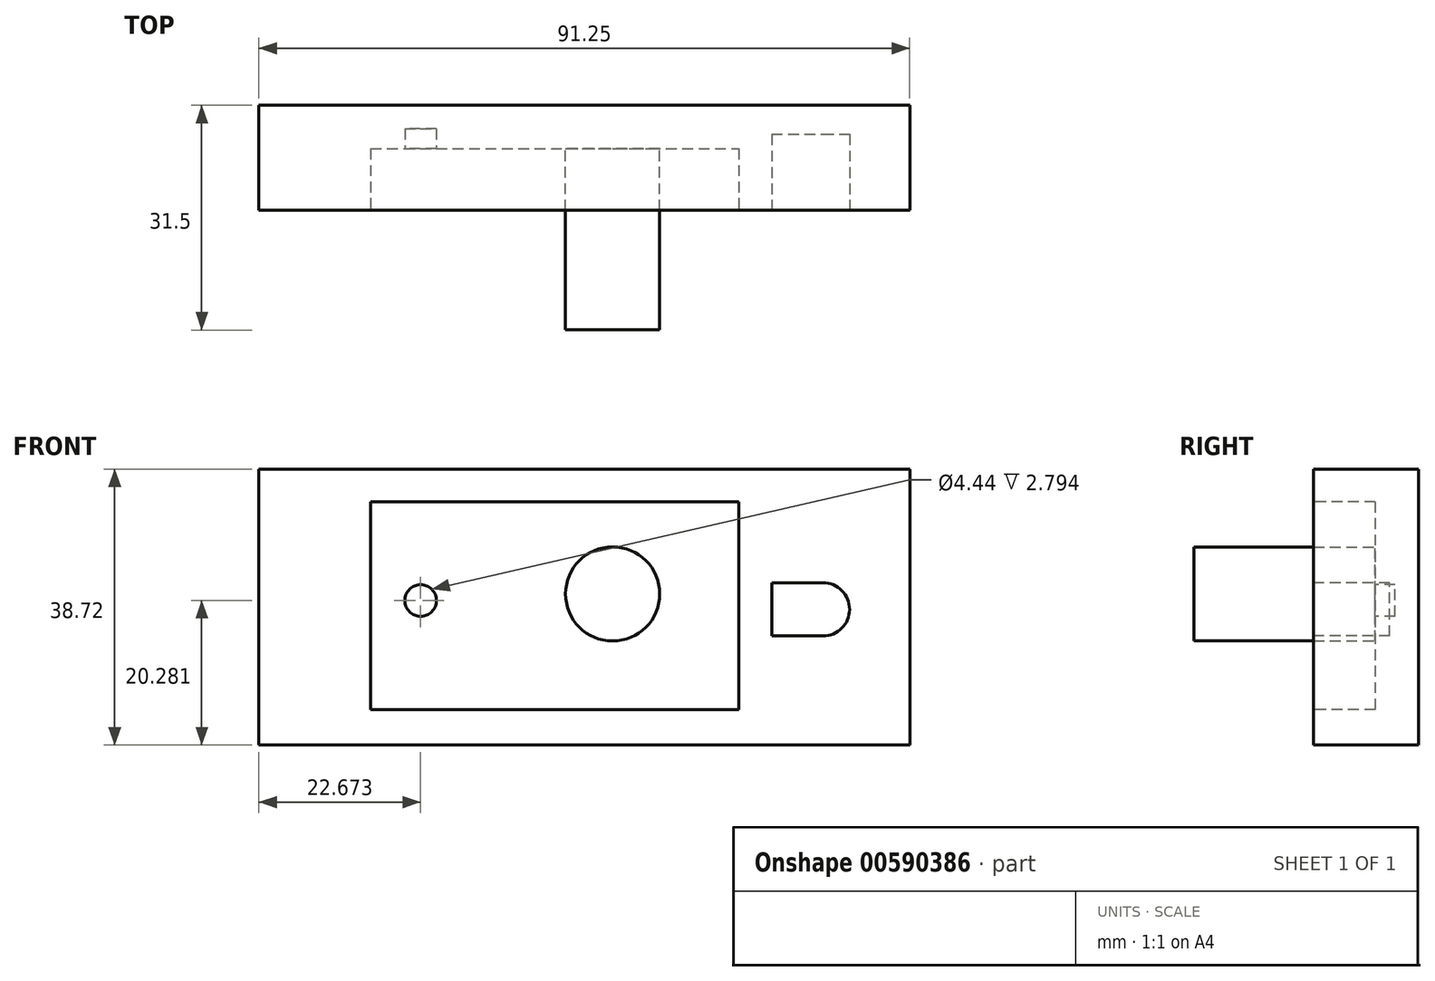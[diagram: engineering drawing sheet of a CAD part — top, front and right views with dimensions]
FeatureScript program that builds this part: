
annotation { "Feature Type Name" : "Feature", "Feature Type Description" : "" }
export const myFeature = defineFeature(function(context is Context, id is Id, definition is map)
    precondition{}
    {
        {
            var Q0;
            Q0=qCreatedBy(makeId("Front.planeOp"),FACE);
            var sketch = newSketch(context, id + "F0", { "sketchPlane" : qUnion([Q0])});
            skLineSegment(sketch, "E0.bottom", {"start": v(-38.62, 15.95) * mm, "end": v(52.63, 15.95) * mm});
            skLineSegment(sketch, "E0.top", {"start": v(-38.62, -22.77) * mm, "end": v(52.63, -22.77) * mm});
            skLineSegment(sketch, "E0.left", {"start": v(-38.62, 15.95) * mm, "end": v(-38.62, -22.77) * mm});
            skLineSegment(sketch, "E0.right", {"start": v(52.63, 15.95) * mm, "end": v(52.63, -22.77) * mm});
            skSolve(sketch);
        }
        {
            var Q0;
            Q0=makeQuery(id+"F0.imprint","IMPRINT",FACE,{"disambiguationData":[TD([[makeQuery(id+"F0.imprint","IMPRINT",EDGE,{"derivedFrom":sQuery(id+"F0.wireOp",EDGE,"E0.bottom")}),-1.0]])]});
            extrude(context, id + "F1", {"entities" : qUnion([Q0]), "depth" : 14.73 * mm, "offsetDistance" : 25.4 * mm});
        }
        {
            var Q0;
            Q0=makeQuery(id+"F1.opExtrude","CAP_FACE",FACE,{"disambiguationData":[OSD([sQuery(id+"F0.wireOp",EDGE,"E0.bottom"),sQuery(id+"F0.wireOp",EDGE,"E0.top"),sQuery(id+"F0.wireOp",EDGE,"E0.left"),sQuery(id+"F0.wireOp",EDGE,"E0.right")])],"isStart":false});
            var sketch = newSketch(context, id + "F2", { "sketchPlane" : qUnion([Q0])});
            skLineSegment(sketch, "E1.bottom", {"start": v(-22.95, 11.34) * mm, "end": v(28.67, 11.34) * mm});
            skLineSegment(sketch, "E1.top", {"start": v(-22.95, -17.8) * mm, "end": v(28.67, -17.8) * mm});
            skLineSegment(sketch, "E1.left", {"start": v(-22.95, 11.34) * mm, "end": v(-22.95, -17.8) * mm});
            skLineSegment(sketch, "E1.right", {"start": v(28.67, 11.34) * mm, "end": v(28.67, -17.8) * mm});
            skSolve(sketch);
        }
        {
            var Q0;
            Q0=makeQuery(id+"F2.imprint","IMPRINT",FACE,{"disambiguationData":[TD([[makeQuery(id+"F2.imprint","IMPRINT",EDGE,{"derivedFrom":sQuery(id+"F2.wireOp",EDGE,"E1.bottom")}),-1.0]])]});
            extrude(context, id + "F3", {"entities" : qUnion([Q0]), "operationType" : NewBodyOperationType.REMOVE, "oppositeDirection" : true, "depth" : 8.64 * mm, "offsetDistance" : 25.4 * mm});
        }
        {
            var Q0;
            Q0=makeQuery(id+"F3.boolean.opBoolean","COPY",FACE,{"derivedFrom":makeQuery(id+"F3.opExtrude","CAP_FACE",FACE,{"disambiguationData":[OSD([sQuery(id+"F2.wireOp",EDGE,"E1.bottom"),sQuery(id+"F2.wireOp",EDGE,"E1.top"),sQuery(id+"F2.wireOp",EDGE,"E1.left"),sQuery(id+"F2.wireOp",EDGE,"E1.right")])],"isStart":false})});
            var sketch = newSketch(context, id + "F4", { "sketchPlane" : qUnion([Q0])});
            skCircle(sketch, "E2", {"center": v(-15.95, -2.49) * mm, "radius": 2.22 * mm});
            skSolve(sketch);
        }
        {
            var Q0;
            Q0=makeQuery(id+"F4.imprint","IMPRINT",FACE,{"disambiguationData":[TD([[makeQuery(id+"F4.imprint","IMPRINT",EDGE,{"derivedFrom":sQuery(id+"F4.wireOp",EDGE,"E2")}),1.0]])]});
            extrude(context, id + "F5", {"entities" : qUnion([Q0]), "operationType" : NewBodyOperationType.REMOVE, "oppositeDirection" : true, "depth" : 2.8 * mm, "offsetDistance" : 25.4 * mm});
        }
        {
            var Q0;
            Q0=makeQuery(id+"F1.opExtrude","CAP_FACE",FACE,{"disambiguationData":[OSD([sQuery(id+"F0.wireOp",EDGE,"E0.bottom"),sQuery(id+"F0.wireOp",EDGE,"E0.top"),sQuery(id+"F0.wireOp",EDGE,"E0.left"),sQuery(id+"F0.wireOp",EDGE,"E0.right")])],"isStart":false});
            var sketch = newSketch(context, id + "F6", { "sketchPlane" : qUnion([Q0])});
            skLineSegment(sketch, "E3", {"start": v(33.28, -3.23) * mm, "end": v(33.28, 0) * mm});
            skPoint(sketch, "E3.startSnap0", {"position": v(-22.95, -3.23) * mm});
            skLineSegment(sketch, "E4", {"start": v(33.28, 0) * mm, "end": v(33.28, -7.47) * mm});
            skLineSegment(sketch, "E5", {"start": v(33.28, -7.47) * mm, "end": v(40.47, -7.47) * mm});
            skLineSegment(sketch, "E6", {"start": v(33.28, 0) * mm, "end": v(40.47, 0) * mm});
            skArc(sketch, "E7", {"start": v(40.47, 0) * mm, "mid": v(44.2, -3.73) * mm, "end": v(40.47, -7.47) * mm});
            skSolve(sketch);
        }
        {
            var Q0;
            {var subQ1=sQuery(id+"F6.wireOp",EDGE,"E5");Q0=makeQuery(id+"F6.imprint","IMPRINT",FACE,{"disambiguationData":[TD([[makeQuery(id+"F6.imprint","IMPRINT",EDGE,{"derivedFrom":subQ1}),1.0]])]});}
            extrude(context, id + "F7", {"entities" : qUnion([Q0]), "operationType" : NewBodyOperationType.REMOVE, "oppositeDirection" : true, "depth" : 10.67 * mm, "offsetDistance" : 25.4 * mm});
        }
        {
            var Q0;
            Q0=makeQuery(id+"F3.boolean.opBoolean","COPY",FACE,{"derivedFrom":makeQuery(id+"F3.opExtrude","CAP_FACE",FACE,{"disambiguationData":[OSD([sQuery(id+"F2.wireOp",EDGE,"E1.bottom"),sQuery(id+"F2.wireOp",EDGE,"E1.top"),sQuery(id+"F2.wireOp",EDGE,"E1.left"),sQuery(id+"F2.wireOp",EDGE,"E1.right")])],"isStart":false})});
            var sketch = newSketch(context, id + "F8", { "sketchPlane" : qUnion([Q0])});
            skCircle(sketch, "E8", {"center": v(10.97, -1.57) * mm, "radius": 6.6 * mm});
            skSolve(sketch);
        }
        {
            var Q0;
            Q0=makeQuery(id+"F8.imprint","IMPRINT",FACE,{"disambiguationData":[TD([[makeQuery(id+"F8.imprint","IMPRINT",EDGE,{"derivedFrom":sQuery(id+"F8.wireOp",EDGE,"E8")}),1.0]])]});
            extrude(context, id + "F9", {"entities" : qUnion([Q0]), "operationType" : NewBodyOperationType.ADD, "depth" : 25.4 * mm, "offsetDistance" : 25.4 * mm});
        }
    });
